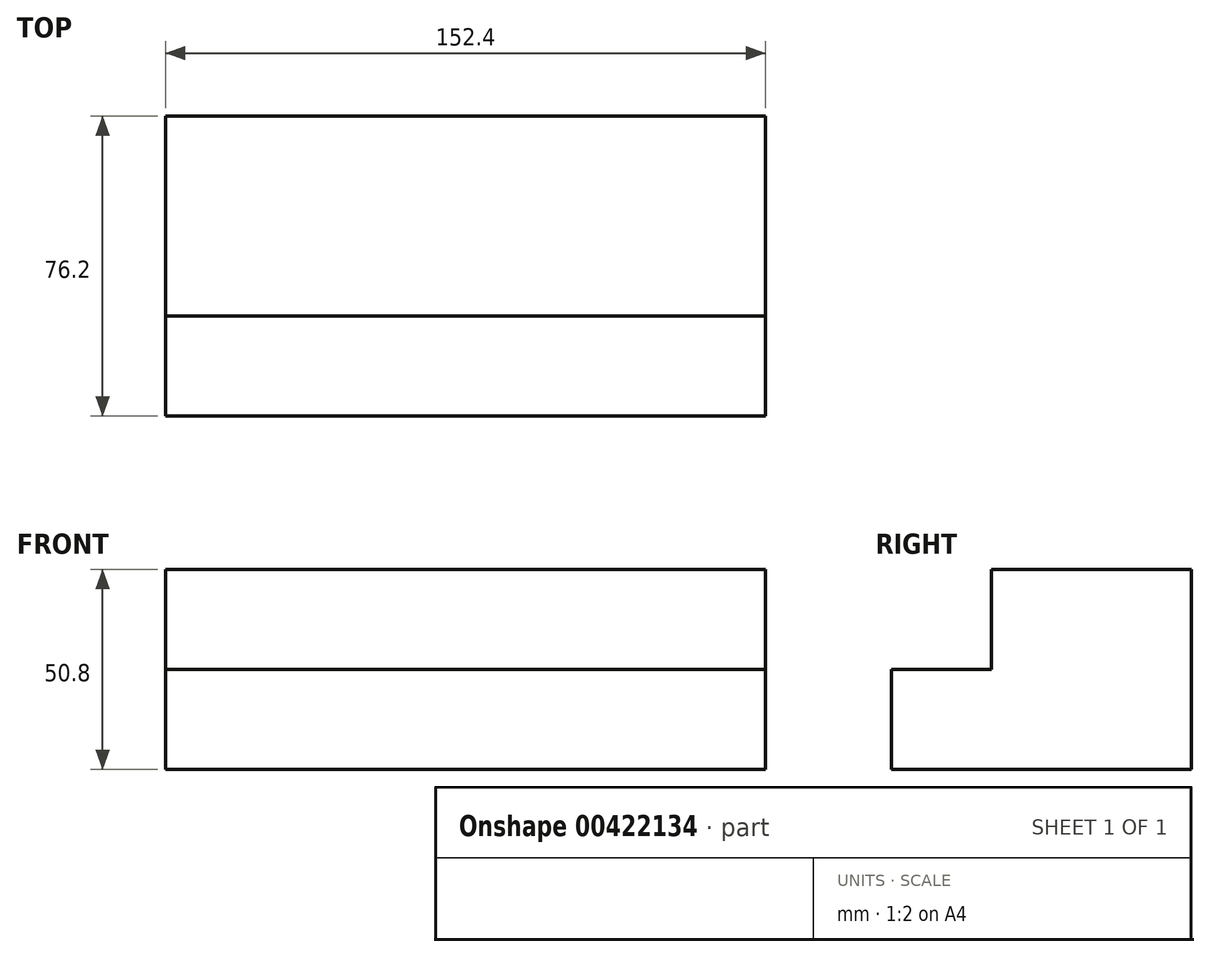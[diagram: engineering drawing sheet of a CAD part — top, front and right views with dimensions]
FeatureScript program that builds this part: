
annotation { "Feature Type Name" : "Feature", "Feature Type Description" : "" }
export const myFeature = defineFeature(function(context is Context, id is Id, definition is map)
    precondition{}
    {
        {
            var Q0;
            Q0=qCreatedBy(makeId("Right.planeOp"),FACE);
            var sketch = newSketch(context, id + "F0", { "sketchPlane" : qUnion([Q0])});
            skLineSegment(sketch, "E0", {"start": v(0, 0) * mm, "end": v(76.2, 0) * mm});
            skLineSegment(sketch, "E1", {"start": v(76.2, 0) * mm, "end": v(76.2, 50.8) * mm});
            skLineSegment(sketch, "E2", {"start": v(76.2, 50.8) * mm, "end": v(25.4, 50.8) * mm});
            skLineSegment(sketch, "E3", {"start": v(25.4, 50.8) * mm, "end": v(25.4, 25.4) * mm});
            skLineSegment(sketch, "E4", {"start": v(25.4, 25.4) * mm, "end": v(0, 25.4) * mm});
            skLineSegment(sketch, "E5", {"start": v(0, 25.4) * mm, "end": v(0, 0) * mm});
            skSolve(sketch);
        }
        {
            var Q0;
            Q0=qCreatedBy(makeId("Right.planeOp"),FACE);
            var sketch = newSketch(context, id + "F1", { "sketchPlane" : qUnion([Q0])});
            skSolve(sketch);
        }
        {
            var Q0;
            Q0 = qSketchRegion(id + "F1", true);
            var Q1;
            Q1=makeQuery(id+"F0.imprint","IMPRINT",FACE,{"disambiguationData":[TD([[makeQuery(id+"F0.imprint","IMPRINT",EDGE,{"derivedFrom":sQuery(id+"F0.wireOp",EDGE,"E0")}),1.0]])]});
            extrude(context, id + "F2", {"entities" : qUnion([Q0, Q1]), "depth" : 152.4 * mm});
        }
    });
